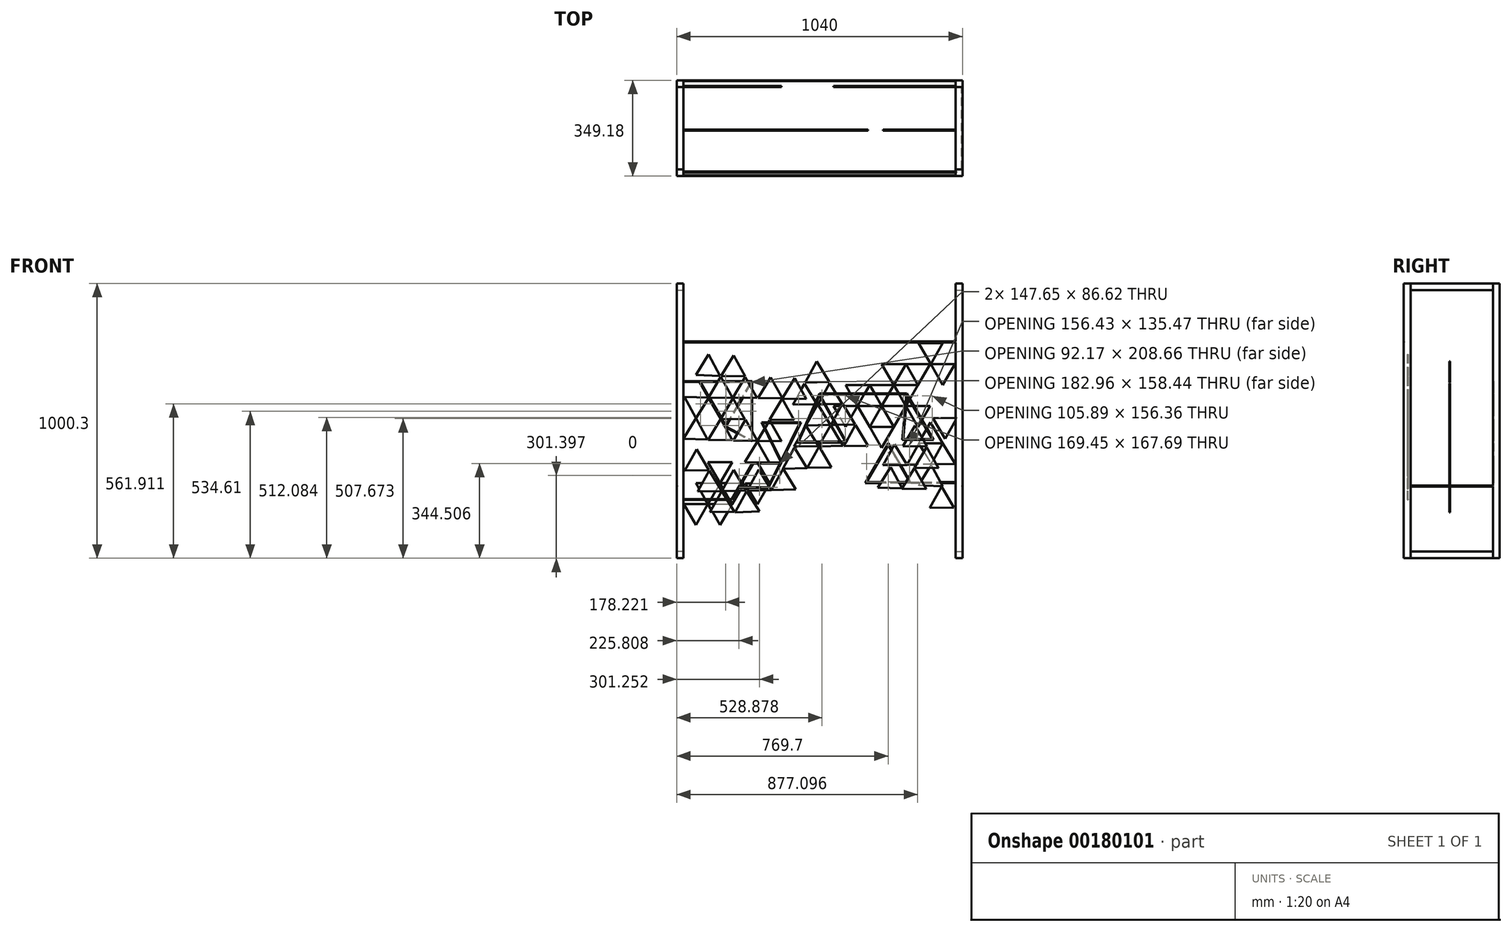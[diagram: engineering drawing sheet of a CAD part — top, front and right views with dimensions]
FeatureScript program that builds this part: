
annotation { "Feature Type Name" : "Feature", "Feature Type Description" : "" }
export const myFeature = defineFeature(function(context is Context, id is Id, definition is map)
    precondition{}
    {
        {
            var Q0;
            Q0=qCreatedBy(makeId("Front.planeOp"),FACE);
            var sketch = newSketch(context, id + "F0", { "sketchPlane" : qUnion([Q0])});
            skLineSegment(sketch, "E0.bottom", {"start": v(500, 500) * mm, "end": v(-500, 500) * mm, "construction": true});
            skLineSegment(sketch, "E0.top", {"start": v(500, -500) * mm, "end": v(-500, -500) * mm, "construction": true});
            skLineSegment(sketch, "E0.left", {"start": v(500, 500) * mm, "end": v(500, -500) * mm, "construction": true});
            skLineSegment(sketch, "E0.right", {"start": v(-500, 500) * mm, "end": v(-500, -500) * mm, "construction": true});
            skPoint(sketch, "E0.middle", {"position": v(0, 0) * mm});
            skCircle(sketch, "E1.cCircle", {"center": v(-269.92, 152.96) * mm, "radius": 25.4 * mm, "construction": true});
            skLineSegment(sketch, "E1.0", {"start": v(-268.9, 203.75) * mm, "end": v(-226.45, 126.67) * mm});
            skLineSegment(sketch, "E1.1", {"start": v(-226.45, 126.67) * mm, "end": v(-314.42, 128.45) * mm});
            skLineSegment(sketch, "E1.2", {"start": v(-314.42, 128.45) * mm, "end": v(-268.9, 203.75) * mm});
            skPoint(sketch, "E1.0.midPoint", {"position": v(-247.67, 165.2) * mm});
            skCircle(sketch, "E2.cCircle", {"center": v(-360.87, 155.69) * mm, "radius": 25.4 * mm, "construction": true});
            skLineSegment(sketch, "E2.0", {"start": v(-359.99, 206.48) * mm, "end": v(-317.33, 129.52) * mm});
            skLineSegment(sketch, "E2.1", {"start": v(-317.33, 129.52) * mm, "end": v(-405.3, 131.05) * mm});
            skLineSegment(sketch, "E2.2", {"start": v(-405.3, 131.05) * mm, "end": v(-359.99, 206.48) * mm});
            skPoint(sketch, "E2.0.midPoint", {"position": v(-338.66, 168) * mm});
            skCircle(sketch, "E3.cCircle", {"center": v(-450.9, 158.41) * mm, "radius": 25.4 * mm, "construction": true});
            skLineSegment(sketch, "E3.0", {"start": v(-449.97, 209.2) * mm, "end": v(-407.39, 132.2) * mm});
            skLineSegment(sketch, "E3.1", {"start": v(-407.39, 132.2) * mm, "end": v(-495.36, 133.83) * mm});
            skLineSegment(sketch, "E3.2", {"start": v(-495.36, 133.83) * mm, "end": v(-449.97, 209.2) * mm});
            skPoint(sketch, "E3.0.midPoint", {"position": v(-428.68, 170.7) * mm});
            skCircle(sketch, "E4.cCircle", {"center": v(-227.18, 73.83) * mm, "radius": 25.4 * mm, "construction": true});
            skLineSegment(sketch, "E4.0", {"start": v(-226.18, 124.62) * mm, "end": v(-183.7, 47.57) * mm});
            skLineSegment(sketch, "E4.1", {"start": v(-183.7, 47.57) * mm, "end": v(-271.67, 49.3) * mm});
            skLineSegment(sketch, "E4.2", {"start": v(-271.67, 49.3) * mm, "end": v(-226.18, 124.62) * mm});
            skPoint(sketch, "E4.0.midPoint", {"position": v(-204.94, 86.1) * mm});
            skCircle(sketch, "E5.cCircle", {"center": v(-182.62, 151.14) * mm, "radius": 25.4 * mm, "construction": true});
            skLineSegment(sketch, "E5.0", {"start": v(-181.92, 201.93) * mm, "end": v(-138.97, 125.14) * mm});
            skLineSegment(sketch, "E5.1", {"start": v(-138.97, 125.14) * mm, "end": v(-226.95, 126.34) * mm});
            skLineSegment(sketch, "E5.2", {"start": v(-226.95, 126.34) * mm, "end": v(-181.92, 201.93) * mm});
            skPoint(sketch, "E5.0.midPoint", {"position": v(-160.45, 163.54) * mm});
            skCircle(sketch, "E6.cCircle", {"center": v(-137.14, 229.35) * mm, "radius": 25.4 * mm, "construction": true});
            skLineSegment(sketch, "E6.0", {"start": v(-136.43, 280.15) * mm, "end": v(-93.51, 203.33) * mm});
            skLineSegment(sketch, "E6.1", {"start": v(-93.51, 203.33) * mm, "end": v(-181.49, 204.57) * mm});
            skLineSegment(sketch, "E6.2", {"start": v(-181.49, 204.57) * mm, "end": v(-136.43, 280.15) * mm});
            skPoint(sketch, "E6.0.midPoint", {"position": v(-114.97, 241.74) * mm});
            skCircle(sketch, "E7.cCircle", {"center": v(-91.67, 304.84) * mm, "radius": 25.4 * mm, "construction": true});
            skLineSegment(sketch, "E7.0", {"start": v(-91.04, 355.63) * mm, "end": v(-48, 278.9) * mm});
            skLineSegment(sketch, "E7.1", {"start": v(-48, 278.9) * mm, "end": v(-135.97, 279.98) * mm});
            skLineSegment(sketch, "E7.2", {"start": v(-135.97, 279.98) * mm, "end": v(-91.04, 355.63) * mm});
            skPoint(sketch, "E7.0.midPoint", {"position": v(-69.52, 317.27) * mm});
            skCircle(sketch, "E8.cCircle", {"center": v(-178.98, 307.57) * mm, "radius": 25.4 * mm, "construction": true});
            skLineSegment(sketch, "E8.0", {"start": v(-178.2, 358.36) * mm, "end": v(-135.38, 281.5) * mm});
            skLineSegment(sketch, "E8.1", {"start": v(-135.38, 281.5) * mm, "end": v(-223.36, 282.85) * mm});
            skLineSegment(sketch, "E8.2", {"start": v(-223.36, 282.85) * mm, "end": v(-178.2, 358.36) * mm});
            skPoint(sketch, "E8.0.midPoint", {"position": v(-156.79, 319.93) * mm});
            skCircle(sketch, "E9.cCircle", {"center": v(-315.4, 231.17) * mm, "radius": 25.4 * mm, "construction": true});
            skLineSegment(sketch, "E9.0", {"start": v(-314.62, 281.96) * mm, "end": v(-271.8, 205.1) * mm});
            skLineSegment(sketch, "E9.1", {"start": v(-271.8, 205.1) * mm, "end": v(-359.78, 206.45) * mm});
            skLineSegment(sketch, "E9.2", {"start": v(-359.78, 206.45) * mm, "end": v(-314.62, 281.96) * mm});
            skPoint(sketch, "E9.0.midPoint", {"position": v(-293.2, 243.53) * mm});
            skCircle(sketch, "E10.cCircle", {"center": v(-270.83, 308.48) * mm, "radius": 25.4 * mm, "construction": true});
            skLineSegment(sketch, "E10.0", {"start": v(-270.06, 359.27) * mm, "end": v(-227.23, 282.4) * mm});
            skLineSegment(sketch, "E10.1", {"start": v(-227.23, 282.4) * mm, "end": v(-315.21, 283.75) * mm});
            skLineSegment(sketch, "E10.2", {"start": v(-315.21, 283.75) * mm, "end": v(-270.06, 359.27) * mm});
            skPoint(sketch, "E10.0.midPoint", {"position": v(-248.64, 320.84) * mm});
            skCircle(sketch, "E11.cCircle", {"center": v(-313.58, 387.6) * mm, "radius": 25.4 * mm, "construction": true});
            skLineSegment(sketch, "E11.0", {"start": v(-312.67, 438.4) * mm, "end": v(-270.05, 361.42) * mm});
            skLineSegment(sketch, "E11.1", {"start": v(-270.05, 361.42) * mm, "end": v(-358.02, 363) * mm});
            skLineSegment(sketch, "E11.2", {"start": v(-358.02, 363) * mm, "end": v(-312.67, 438.4) * mm});
            skPoint(sketch, "E11.0.midPoint", {"position": v(-291.36, 399.9) * mm});
            skCircle(sketch, "E12.cCircle", {"center": v(-359.96, 309.39) * mm, "radius": 25.4 * mm, "construction": true});
            skLineSegment(sketch, "E12.0", {"start": v(-359.14, 360.18) * mm, "end": v(-316.38, 283.28) * mm});
            skLineSegment(sketch, "E12.1", {"start": v(-316.38, 283.28) * mm, "end": v(-404.36, 284.7) * mm});
            skLineSegment(sketch, "E12.2", {"start": v(-404.36, 284.7) * mm, "end": v(-359.14, 360.18) * mm});
            skPoint(sketch, "E12.0.midPoint", {"position": v(-337.76, 321.73) * mm});
            skCircle(sketch, "E13.cCircle", {"center": v(-448.25, 259.98) * mm, "radius": 25.4 * mm, "construction": true});
            skLineSegment(sketch, "E13.0", {"start": v(-403.42, 283.87) * mm, "end": v(-449.97, 209.2) * mm});
            skLineSegment(sketch, "E13.1", {"start": v(-449.97, 209.2) * mm, "end": v(-491.36, 286.85) * mm});
            skLineSegment(sketch, "E13.2", {"start": v(-491.36, 286.85) * mm, "end": v(-403.42, 283.87) * mm});
            skPoint(sketch, "E13.0.midPoint", {"position": v(-426.7, 246.54) * mm});
            skCircle(sketch, "E14.cCircle", {"center": v(-405.43, 390.33) * mm, "radius": 25.4 * mm, "construction": true});
            skLineSegment(sketch, "E14.0", {"start": v(-403.66, 441.1) * mm, "end": v(-362.36, 363.4) * mm});
            skLineSegment(sketch, "E14.1", {"start": v(-362.36, 363.4) * mm, "end": v(-450.29, 366.48) * mm});
            skLineSegment(sketch, "E14.2", {"start": v(-450.29, 366.48) * mm, "end": v(-403.66, 441.1) * mm});
            skPoint(sketch, "E14.0.midPoint", {"position": v(-383, 402.25) * mm});
            skCircle(sketch, "E15.cCircle", {"center": v(389.15, 53.61) * mm, "radius": 25.4 * mm, "construction": true});
            skLineSegment(sketch, "E15.0", {"start": v(389.72, 104.4) * mm, "end": v(432.85, 27.72) * mm});
            skLineSegment(sketch, "E15.1", {"start": v(432.85, 27.72) * mm, "end": v(344.87, 28.71) * mm});
            skLineSegment(sketch, "E15.2", {"start": v(344.87, 28.71) * mm, "end": v(389.72, 104.4) * mm});
            skPoint(sketch, "E15.0.midPoint", {"position": v(411.29, 66.06) * mm});
            skCircle(sketch, "E16.cCircle", {"center": v(456.43, 185.05) * mm, "radius": 25.4 * mm, "construction": true});
            skLineSegment(sketch, "E16.0", {"start": v(412.02, 209.72) * mm, "end": v(500, 211.17) * mm});
            skLineSegment(sketch, "E16.1", {"start": v(500, 211.17) * mm, "end": v(457.27, 134.26) * mm});
            skLineSegment(sketch, "E16.2", {"start": v(457.27, 134.26) * mm, "end": v(412.02, 209.72) * mm});
            skPoint(sketch, "E16.0.midPoint", {"position": v(456.01, 210.45) * mm});
            skCircle(sketch, "E17.cCircle", {"center": v(347.31, 131.83) * mm, "radius": 25.4 * mm, "construction": true});
            skLineSegment(sketch, "E17.0", {"start": v(348.1, 182.62) * mm, "end": v(390.91, 105.75) * mm});
            skLineSegment(sketch, "E17.1", {"start": v(390.91, 105.75) * mm, "end": v(302.93, 107.1) * mm});
            skLineSegment(sketch, "E17.2", {"start": v(302.93, 107.1) * mm, "end": v(348.1, 182.62) * mm});
            skPoint(sketch, "E17.0.midPoint", {"position": v(369.5, 144.19) * mm});
            skCircle(sketch, "E18.cCircle", {"center": v(344.43, -22.63) * mm, "radius": 25.4 * mm, "construction": true});
            skLineSegment(sketch, "E18.0", {"start": v(345.1, 28.16) * mm, "end": v(388.08, -48.61) * mm});
            skLineSegment(sketch, "E18.1", {"start": v(388.08, -48.61) * mm, "end": v(300.1, -47.45) * mm});
            skLineSegment(sketch, "E18.2", {"start": v(300.1, -47.45) * mm, "end": v(345.1, 28.16) * mm});
            skPoint(sketch, "E18.0.midPoint", {"position": v(366.6, -10.22) * mm});
            skCircle(sketch, "E19.cCircle", {"center": v(257.12, -19.9) * mm, "radius": 25.4 * mm, "construction": true});
            skLineSegment(sketch, "E19.0", {"start": v(258.54, 30.88) * mm, "end": v(300.39, -46.53) * mm});
            skLineSegment(sketch, "E19.1", {"start": v(300.39, -46.53) * mm, "end": v(212.43, -44.06) * mm});
            skLineSegment(sketch, "E19.2", {"start": v(212.43, -44.06) * mm, "end": v(258.54, 30.88) * mm});
            skPoint(sketch, "E19.0.midPoint", {"position": v(279.47, -7.83) * mm});
            skSolve(sketch);
        }
        {
            var Q0;
            Q0=makeQuery(id+"F0.imprint","IMPRINT",FACE,{"disambiguationData":[TD([[makeQuery(id+"F0.imprint","IMPRINT",EDGE,{"derivedFrom":sQuery(id+"F0.wireOp",EDGE,"E14.0")}),-1.0]])]});
            var Q1;
            Q1=makeQuery(id+"F0.imprint","IMPRINT",FACE,{"disambiguationData":[TD([[makeQuery(id+"F0.imprint","IMPRINT",EDGE,{"derivedFrom":sQuery(id+"F0.wireOp",EDGE,"E11.0")}),-1.0]])]});
            var Q2;
            Q2=makeQuery(id+"F0.imprint","IMPRINT",FACE,{"disambiguationData":[TD([[makeQuery(id+"F0.imprint","IMPRINT",EDGE,{"derivedFrom":sQuery(id+"F0.wireOp",EDGE,"E12.0")}),-1.0]])]});
            var Q3;
            Q3=makeQuery(id+"F0.imprint","IMPRINT",FACE,{"disambiguationData":[TD([[makeQuery(id+"F0.imprint","IMPRINT",EDGE,{"derivedFrom":sQuery(id+"F0.wireOp",EDGE,"E13.0")}),-1.0]])]});
            var Q4;
            Q4=makeQuery(id+"F0.imprint","IMPRINT",FACE,{"disambiguationData":[TD([[makeQuery(id+"F0.imprint","IMPRINT",EDGE,{"derivedFrom":sQuery(id+"F0.wireOp",EDGE,"E3.0")}),-1.0]])]});
            var Q5;
            Q5=makeQuery(id+"F0.imprint","IMPRINT",FACE,{"disambiguationData":[TD([[makeQuery(id+"F0.imprint","IMPRINT",EDGE,{"derivedFrom":sQuery(id+"F0.wireOp",EDGE,"E2.0")}),-1.0]])]});
            var Q6;
            Q6=makeQuery(id+"F0.imprint","IMPRINT",FACE,{"disambiguationData":[TD([[makeQuery(id+"F0.imprint","IMPRINT",EDGE,{"derivedFrom":sQuery(id+"F0.wireOp",EDGE,"E9.0")}),-1.0]])]});
            var Q7;
            Q7=makeQuery(id+"F0.imprint","IMPRINT",FACE,{"disambiguationData":[TD([[makeQuery(id+"F0.imprint","IMPRINT",EDGE,{"derivedFrom":sQuery(id+"F0.wireOp",EDGE,"E10.0")}),-1.0]])]});
            var Q8;
            Q8=makeQuery(id+"F0.imprint","IMPRINT",FACE,{"disambiguationData":[TD([[makeQuery(id+"F0.imprint","IMPRINT",EDGE,{"derivedFrom":sQuery(id+"F0.wireOp",EDGE,"E8.0")}),-1.0]])]});
            var Q9;
            Q9=makeQuery(id+"F0.imprint","IMPRINT",FACE,{"disambiguationData":[TD([[makeQuery(id+"F0.imprint","IMPRINT",EDGE,{"derivedFrom":sQuery(id+"F0.wireOp",EDGE,"E7.0")}),-1.0]])]});
            var Q10;
            Q10=makeQuery(id+"F0.imprint","IMPRINT",FACE,{"disambiguationData":[TD([[makeQuery(id+"F0.imprint","IMPRINT",EDGE,{"derivedFrom":sQuery(id+"F0.wireOp",EDGE,"E6.0")}),-1.0]])]});
            var Q11;
            {var subQ1=sQuery(id+"F0.wireOp",EDGE,"E5.0");Q11=makeQuery(id+"F0.imprint","IMPRINT",FACE,{"disambiguationData":[TD([[makeQuery(id+"F0.imprint","IMPRINT",EDGE,{"derivedFrom":subQ1}),-1.0]])]});}
            var Q12;
            {var subQ0=sQuery(id+"F0.wireOp",EDGE,"E1.2");Q12=makeQuery(id+"F0.imprint","IMPRINT",FACE,{"disambiguationData":[TD([[makeQuery(id+"F0.imprint","IMPRINT",EDGE,{"derivedFrom":subQ0}),-1.0]])]});}
            var Q13;
            Q13=makeQuery(id+"F0.imprint","IMPRINT",FACE,{"disambiguationData":[TD([[makeQuery(id+"F0.imprint","IMPRINT",EDGE,{"derivedFrom":sQuery(id+"F0.wireOp",EDGE,"E4.0")}),-1.0]])]});
            var Q14;
            Q14=makeQuery(id+"F0.imprint","IMPRINT",FACE,{"disambiguationData":[TD([[makeQuery(id+"F0.imprint","IMPRINT",EDGE,{"derivedFrom":sQuery(id+"F0.wireOp",EDGE,"E17.0")}),-1.0]])]});
            var Q15;
            Q15=makeQuery(id+"F0.imprint","IMPRINT",FACE,{"disambiguationData":[TD([[makeQuery(id+"F0.imprint","IMPRINT",EDGE,{"derivedFrom":sQuery(id+"F0.wireOp",EDGE,"E16.0")}),-1.0]])]});
            var Q16;
            Q16=makeQuery(id+"F0.imprint","IMPRINT",FACE,{"disambiguationData":[TD([[makeQuery(id+"F0.imprint","IMPRINT",EDGE,{"derivedFrom":sQuery(id+"F0.wireOp",EDGE,"E15.0")}),-1.0]])]});
            var Q17;
            Q17=makeQuery(id+"F0.imprint","IMPRINT",FACE,{"disambiguationData":[TD([[makeQuery(id+"F0.imprint","IMPRINT",EDGE,{"derivedFrom":sQuery(id+"F0.wireOp",EDGE,"E18.0")}),-1.0]])]});
            var Q18;
            Q18=makeQuery(id+"F0.imprint","IMPRINT",FACE,{"disambiguationData":[TD([[makeQuery(id+"F0.imprint","IMPRINT",EDGE,{"derivedFrom":sQuery(id+"F0.wireOp",EDGE,"E19.0")}),-1.0]])]});
            extrude(context, id + "F1", {"entities" : qUnion([Q0, Q1, Q2, Q3, Q4, Q5, Q6, Q7, Q8, Q9, Q10, Q11, Q12, Q13, Q14, Q15, Q16, Q17, Q18]), "depth" : 3 * mm});
        }
        {
            var Q0;
            Q0=qCreatedBy(makeId("Top.planeOp"),FACE);
            cPlane(context, id + "F2", {"entities" : qUnion([Q0]), "cplaneType" : CPlaneType.OFFSET, "offset" : 500 * mm, "width" : 152.4 * mm, "height" : 152.4 * mm});
        }
        {
            var Q0;
            Q0=qCreatedBy(id+"F2.planeOp",FACE);
            var sketch = newSketch(context, id + "F3", { "sketchPlane" : qUnion([Q0])});
            skLineSegment(sketch, "E20.bottom", {"start": v(-520, 8.18) * mm, "end": v(-495, 8.18) * mm});
            skLineSegment(sketch, "E20.top", {"start": v(-520, -16.82) * mm, "end": v(-495, -16.82) * mm});
            skLineSegment(sketch, "E20.left", {"start": v(-520, 8.18) * mm, "end": v(-520, -16.82) * mm});
            skLineSegment(sketch, "E20.right", {"start": v(-495, 8.18) * mm, "end": v(-495, -16.82) * mm});
            skLineSegment(sketch, "E21", {"start": v(0, 81.2) * mm, "end": v(0, -142.37) * mm, "construction": true});
            skLineSegment(sketch, "E22.MirrorCS", {"start": v(520, -16.82) * mm, "end": v(495, -16.82) * mm});
            skLineSegment(sketch, "E23.MirrorCS", {"start": v(495, 8.18) * mm, "end": v(495, -16.82) * mm});
            skLineSegment(sketch, "E24.MirrorCS", {"start": v(520, 8.18) * mm, "end": v(495, 8.18) * mm});
            skLineSegment(sketch, "E25.MirrorCS", {"start": v(520, 8.18) * mm, "end": v(520, -16.82) * mm});
            skSolve(sketch);
        }
        {
            var Q0;
            Q0 = qSketchRegion(id + "F3", true);
            extrude(context, id + "F4", {"entities" : qUnion([Q0]), "oppositeDirection" : true, "depth" : 800 * mm, "hasSecondDirection" : true, "secondDirectionOppositeDirection" : false, "secondDirectionDepth" : 200 * mm});
        }
        {
            var Q0;
            Q0=makeQuery(id+"F4.opExtrude","SWEPT_FACE",FACE,{"disambiguationData":[OSD([sQuery(id+"F3.wireOp",EDGE,"E20.bottom")])]});
            var sketch = newSketch(context, id + "F5", { "sketchPlane" : qUnion([Q0])});
            skLineSegment(sketch, "E26.bottom", {"start": v(-495.28, -300.3) * mm, "end": v(-519.46, -300.3) * mm});
            skLineSegment(sketch, "E26.top", {"start": v(-495.28, -276.12) * mm, "end": v(-519.46, -276.12) * mm});
            skLineSegment(sketch, "E26.left", {"start": v(-495.28, -300.3) * mm, "end": v(-495.28, -276.12) * mm});
            skLineSegment(sketch, "E26.right", {"start": v(-519.46, -300.3) * mm, "end": v(-519.46, -276.12) * mm});
            skLineSegment(sketch, "E27", {"start": v(0, 0) * mm, "end": v(0, -471.83) * mm, "construction": true});
            skLineSegment(sketch, "E28.MirrorCS", {"start": v(495.28, -276.12) * mm, "end": v(519.46, -276.12) * mm});
            skLineSegment(sketch, "E29.MirrorCS", {"start": v(495.28, -300.3) * mm, "end": v(495.28, -276.12) * mm});
            skLineSegment(sketch, "E30.MirrorCS", {"start": v(495.28, -300.3) * mm, "end": v(519.46, -300.3) * mm});
            skLineSegment(sketch, "E31.MirrorCS", {"start": v(519.46, -300.3) * mm, "end": v(519.46, -276.12) * mm});
            skSolve(sketch);
        }
        {
            var Q0;
            Q0=makeQuery(id+"F5.imprint","IMPRINT",FACE,{"disambiguationData":[TD([[makeQuery(id+"F5.imprint","IMPRINT",EDGE,{"derivedFrom":sQuery(id+"F5.wireOp",EDGE,"E26.bottom")}),-1.0]])]});
            var Q1;
            {var subQ0=sQuery(id+"F5.wireOp",EDGE,"E28.MirrorCS");Q1=makeQuery(id+"F5.imprint","IMPRINT",FACE,{"disambiguationData":[TD([[makeQuery(id+"F5.imprint","IMPRINT",EDGE,{"derivedFrom":subQ0}),-1.0]])]});}
            extrude(context, id + "F6", {"entities" : qUnion([Q0, Q1]), "depth" : 300 * mm});
        }
        {
            var Q0;
            Q0=makeQuery(id+"F6.opExtrude","SWEPT_FACE",FACE,{"disambiguationData":[OSD([sQuery(id+"F5.wireOp",EDGE,"E26.bottom")])]});
            var sketch = newSketch(context, id + "F7", { "sketchPlane" : qUnion([Q0])});
            skLineSegment(sketch, "E32.bottom", {"start": v(-519.86, -308.03) * mm, "end": v(-495.5, -308.03) * mm});
            skLineSegment(sketch, "E32.top", {"start": v(-519.86, -332.36) * mm, "end": v(-495.5, -332.36) * mm});
            skLineSegment(sketch, "E32.left", {"start": v(-519.86, -308.03) * mm, "end": v(-519.86, -332.36) * mm});
            skLineSegment(sketch, "E32.right", {"start": v(-495.5, -308.03) * mm, "end": v(-495.5, -332.36) * mm});
            skLineSegment(sketch, "E33", {"start": v(0, 0) * mm, "end": v(0, -208.74) * mm, "construction": true});
            skLineSegment(sketch, "E34.MirrorCS", {"start": v(519.86, -308.03) * mm, "end": v(495.5, -308.03) * mm});
            skLineSegment(sketch, "E35.MirrorCS", {"start": v(519.86, -332.36) * mm, "end": v(495.5, -332.36) * mm});
            skLineSegment(sketch, "E36.MirrorCS", {"start": v(495.5, -308.03) * mm, "end": v(495.5, -332.36) * mm});
            skLineSegment(sketch, "E37.MirrorCS", {"start": v(519.86, -308.03) * mm, "end": v(519.86, -332.36) * mm});
            skSolve(sketch);
        }
        {
            var Q0;
            {var subQ2=sQuery(id+"F7.wireOp",EDGE,"E35.MirrorCS");Q0=makeQuery(id+"F7.imprint","IMPRINT",FACE,{"disambiguationData":[TD([[makeQuery(id+"F7.imprint","IMPRINT",EDGE,{"derivedFrom":subQ2}),-1.0]])]});}
            var Q1;
            Q1=makeQuery(id+"F7.imprint","IMPRINT",FACE,{"disambiguationData":[TD([[makeQuery(id+"F7.imprint","IMPRINT",EDGE,{"derivedFrom":sQuery(id+"F7.wireOp",EDGE,"E32.bottom")}),-1.0]])]});
            extrude(context, id + "F8", {"entities" : qUnion([Q0, Q1]), "oppositeDirection" : true, "depth" : 1000 * mm});
        }
        {
            var Q0;
            Q0=makeQuery(id+"F8.opExtrude","SWEPT_FACE",FACE,{"disambiguationData":[OSD([sQuery(id+"F5.wireOp",EDGE,"E26.bottom")])]});
            var sketch = newSketch(context, id + "F9", { "sketchPlane" : qUnion([Q0])});
            skCircle(sketch, "E38.cCircle", {"center": v(138.38, 304.83) * mm, "radius": 25.4 * mm, "construction": true});
            skLineSegment(sketch, "E38.0", {"start": v(94.39, 330.23) * mm, "end": v(182.38, 330.23) * mm});
            skLineSegment(sketch, "E38.1", {"start": v(182.38, 330.23) * mm, "end": v(138.38, 254.03) * mm});
            skLineSegment(sketch, "E38.2", {"start": v(138.38, 254.03) * mm, "end": v(94.39, 330.23) * mm});
            skPoint(sketch, "E38.0.midPoint", {"position": v(138.38, 330.23) * mm});
            skCircle(sketch, "E39.cCircle", {"center": v(226.37, 304.83) * mm, "radius": 25.4 * mm, "construction": true});
            skLineSegment(sketch, "E39.0", {"start": v(182.38, 330.23) * mm, "end": v(270.37, 330.23) * mm});
            skLineSegment(sketch, "E39.1", {"start": v(270.37, 330.23) * mm, "end": v(226.37, 254.03) * mm});
            skLineSegment(sketch, "E39.2", {"start": v(226.37, 254.03) * mm, "end": v(182.38, 330.23) * mm});
            skPoint(sketch, "E39.0.midPoint", {"position": v(226.37, 330.23) * mm});
            skCircle(sketch, "E40.cCircle", {"center": v(182.38, 228.63) * mm, "radius": 25.4 * mm, "construction": true});
            skLineSegment(sketch, "E40.0", {"start": v(138.38, 254.03) * mm, "end": v(226.37, 254.03) * mm});
            skLineSegment(sketch, "E40.1", {"start": v(226.37, 254.03) * mm, "end": v(182.38, 177.83) * mm});
            skLineSegment(sketch, "E40.2", {"start": v(182.38, 177.83) * mm, "end": v(138.38, 254.03) * mm});
            skPoint(sketch, "E40.0.midPoint", {"position": v(182.38, 254.03) * mm});
            skCircle(sketch, "E41.cCircle", {"center": v(226.37, 152.43) * mm, "radius": 25.4 * mm, "construction": true});
            skLineSegment(sketch, "E41.0", {"start": v(182.38, 177.83) * mm, "end": v(270.37, 177.83) * mm});
            skLineSegment(sketch, "E41.1", {"start": v(270.37, 177.83) * mm, "end": v(226.37, 101.63) * mm});
            skLineSegment(sketch, "E41.2", {"start": v(226.37, 101.63) * mm, "end": v(182.38, 177.83) * mm});
            skPoint(sketch, "E41.0.midPoint", {"position": v(226.37, 177.83) * mm});
            skCircle(sketch, "E42.cCircle", {"center": v(94.39, 228.63) * mm, "radius": 25.4 * mm, "construction": true});
            skLineSegment(sketch, "E42.0", {"start": v(50.4, 254.03) * mm, "end": v(138.38, 254.03) * mm});
            skLineSegment(sketch, "E42.1", {"start": v(138.38, 254.03) * mm, "end": v(94.39, 177.83) * mm});
            skLineSegment(sketch, "E42.2", {"start": v(94.39, 177.83) * mm, "end": v(50.4, 254.03) * mm});
            skPoint(sketch, "E42.0.midPoint", {"position": v(94.39, 254.03) * mm});
            skCircle(sketch, "E43.cCircle", {"center": v(270.37, 228.63) * mm, "radius": 25.4 * mm, "construction": true});
            skLineSegment(sketch, "E43.0", {"start": v(226.37, 254.03) * mm, "end": v(314.36, 254.03) * mm});
            skLineSegment(sketch, "E43.1", {"start": v(314.36, 254.03) * mm, "end": v(270.37, 177.83) * mm});
            skLineSegment(sketch, "E43.2", {"start": v(270.37, 177.83) * mm, "end": v(226.37, 254.03) * mm});
            skPoint(sketch, "E43.0.midPoint", {"position": v(270.37, 254.03) * mm});
            skCircle(sketch, "E44.cCircle", {"center": v(314.36, 304.83) * mm, "radius": 25.4 * mm, "construction": true});
            skLineSegment(sketch, "E44.0", {"start": v(270.37, 330.23) * mm, "end": v(358.35, 330.23) * mm});
            skLineSegment(sketch, "E44.1", {"start": v(358.35, 330.23) * mm, "end": v(314.36, 254.03) * mm});
            skLineSegment(sketch, "E44.2", {"start": v(314.36, 254.03) * mm, "end": v(270.37, 330.23) * mm});
            skPoint(sketch, "E44.0.midPoint", {"position": v(314.36, 330.23) * mm});
            skCircle(sketch, "E45.cCircle", {"center": v(358.35, 228.63) * mm, "radius": 25.4 * mm, "construction": true});
            skLineSegment(sketch, "E45.0", {"start": v(314.36, 254.03) * mm, "end": v(402.35, 254.03) * mm});
            skLineSegment(sketch, "E45.1", {"start": v(402.35, 254.03) * mm, "end": v(358.35, 177.83) * mm});
            skLineSegment(sketch, "E45.2", {"start": v(358.35, 177.83) * mm, "end": v(314.36, 254.03) * mm});
            skPoint(sketch, "E45.0.midPoint", {"position": v(358.35, 254.03) * mm});
            skCircle(sketch, "E46.cCircle", {"center": v(270.37, 381.03) * mm, "radius": 25.4 * mm, "construction": true});
            skLineSegment(sketch, "E46.0", {"start": v(226.37, 406.43) * mm, "end": v(314.36, 406.43) * mm});
            skLineSegment(sketch, "E46.1", {"start": v(314.36, 406.43) * mm, "end": v(270.37, 330.23) * mm});
            skLineSegment(sketch, "E46.2", {"start": v(270.37, 330.23) * mm, "end": v(226.37, 406.43) * mm});
            skPoint(sketch, "E46.0.midPoint", {"position": v(270.37, 406.43) * mm});
            skCircle(sketch, "E47.cCircle", {"center": v(358.35, 381.03) * mm, "radius": 25.4 * mm, "construction": true});
            skLineSegment(sketch, "E47.0", {"start": v(314.36, 406.43) * mm, "end": v(402.35, 406.43) * mm});
            skLineSegment(sketch, "E47.1", {"start": v(402.35, 406.43) * mm, "end": v(358.35, 330.23) * mm});
            skLineSegment(sketch, "E47.2", {"start": v(358.35, 330.23) * mm, "end": v(314.36, 406.43) * mm});
            skPoint(sketch, "E47.0.midPoint", {"position": v(358.35, 406.43) * mm});
            skCircle(sketch, "E48.cCircle", {"center": v(448.6, 381.03) * mm, "radius": 25.4 * mm, "construction": true});
            skLineSegment(sketch, "E48.0", {"start": v(404.6, 406.43) * mm, "end": v(492.59, 406.43) * mm});
            skLineSegment(sketch, "E48.1", {"start": v(492.59, 406.43) * mm, "end": v(448.6, 330.23) * mm});
            skLineSegment(sketch, "E48.2", {"start": v(448.6, 330.23) * mm, "end": v(404.6, 406.43) * mm});
            skPoint(sketch, "E48.0.midPoint", {"position": v(448.6, 406.43) * mm});
            skCircle(sketch, "E49.cCircle", {"center": v(404.6, 457.23) * mm, "radius": 25.4 * mm, "construction": true});
            skLineSegment(sketch, "E49.0", {"start": v(360.6, 482.63) * mm, "end": v(448.6, 482.63) * mm});
            skLineSegment(sketch, "E49.1", {"start": v(448.6, 482.63) * mm, "end": v(404.6, 406.43) * mm});
            skLineSegment(sketch, "E49.2", {"start": v(404.6, 406.43) * mm, "end": v(360.6, 482.63) * mm});
            skPoint(sketch, "E49.0.midPoint", {"position": v(404.6, 482.63) * mm});
            skCircle(sketch, "E50.cCircle", {"center": v(-450.1, -128.73) * mm, "radius": 25.4 * mm, "construction": true});
            skLineSegment(sketch, "E50.0", {"start": v(-494.1, -103.33) * mm, "end": v(-406.1, -103.33) * mm});
            skLineSegment(sketch, "E50.1", {"start": v(-406.1, -103.33) * mm, "end": v(-450.1, -179.53) * mm});
            skLineSegment(sketch, "E50.2", {"start": v(-450.1, -179.53) * mm, "end": v(-494.1, -103.33) * mm});
            skPoint(sketch, "E50.0.midPoint", {"position": v(-450.1, -103.33) * mm});
            skCircle(sketch, "E51.cCircle", {"center": v(-406.1, -52.53) * mm, "radius": 25.4 * mm, "construction": true});
            skLineSegment(sketch, "E51.0", {"start": v(-450.1, -27.13) * mm, "end": v(-362.1, -27.13) * mm});
            skLineSegment(sketch, "E51.1", {"start": v(-362.1, -27.13) * mm, "end": v(-406.1, -103.33) * mm});
            skLineSegment(sketch, "E51.2", {"start": v(-406.1, -103.33) * mm, "end": v(-450.1, -27.13) * mm});
            skPoint(sketch, "E51.0.midPoint", {"position": v(-406.1, -27.13) * mm});
            skCircle(sketch, "E52.cCircle", {"center": v(-362.1, -128.73) * mm, "radius": 25.4 * mm, "construction": true});
            skLineSegment(sketch, "E52.0", {"start": v(-406.1, -103.33) * mm, "end": v(-318.12, -103.33) * mm});
            skLineSegment(sketch, "E52.1", {"start": v(-318.12, -103.33) * mm, "end": v(-362.1, -179.53) * mm});
            skLineSegment(sketch, "E52.2", {"start": v(-362.1, -179.53) * mm, "end": v(-406.1, -103.33) * mm});
            skPoint(sketch, "E52.0.midPoint", {"position": v(-362.1, -103.33) * mm});
            skCircle(sketch, "E53.cCircle", {"center": v(-362.1, 23.67) * mm, "radius": 25.4 * mm, "construction": true});
            skLineSegment(sketch, "E53.0", {"start": v(-406.1, 49.07) * mm, "end": v(-318.12, 49.07) * mm});
            skLineSegment(sketch, "E53.1", {"start": v(-318.12, 49.07) * mm, "end": v(-362.1, -27.13) * mm});
            skLineSegment(sketch, "E53.2", {"start": v(-362.1, -27.13) * mm, "end": v(-406.1, 49.07) * mm});
            skPoint(sketch, "E53.0.midPoint", {"position": v(-362.1, 49.07) * mm});
            skCircle(sketch, "E54.cCircle", {"center": v(-318.12, -52.53) * mm, "radius": 25.4 * mm, "construction": true});
            skLineSegment(sketch, "E54.0", {"start": v(-362.1, -27.13) * mm, "end": v(-274.12, -27.13) * mm});
            skLineSegment(sketch, "E54.1", {"start": v(-274.12, -27.13) * mm, "end": v(-318.12, -103.33) * mm});
            skLineSegment(sketch, "E54.2", {"start": v(-318.12, -103.33) * mm, "end": v(-362.1, -27.13) * mm});
            skPoint(sketch, "E54.0.midPoint", {"position": v(-318.12, -27.13) * mm});
            skCircle(sketch, "E55.cCircle", {"center": v(-226.16, -53.53) * mm, "radius": 25.4 * mm, "construction": true});
            skLineSegment(sketch, "E55.0", {"start": v(-270.15, -28.13) * mm, "end": v(-182.16, -28.13) * mm});
            skLineSegment(sketch, "E55.1", {"start": v(-182.16, -28.13) * mm, "end": v(-226.16, -104.33) * mm});
            skLineSegment(sketch, "E55.2", {"start": v(-226.16, -104.33) * mm, "end": v(-270.15, -28.13) * mm});
            skPoint(sketch, "E55.0.midPoint", {"position": v(-226.16, -28.13) * mm});
            skCircle(sketch, "E56.cCircle", {"center": v(-182.16, 22.67) * mm, "radius": 25.4 * mm, "construction": true});
            skLineSegment(sketch, "E56.0", {"start": v(-226.16, 48.07) * mm, "end": v(-138.17, 48.07) * mm});
            skLineSegment(sketch, "E56.1", {"start": v(-138.17, 48.07) * mm, "end": v(-182.16, -28.13) * mm});
            skLineSegment(sketch, "E56.2", {"start": v(-182.16, -28.13) * mm, "end": v(-226.16, 48.07) * mm});
            skPoint(sketch, "E56.0.midPoint", {"position": v(-182.16, 48.07) * mm});
            skSolve(sketch);
        }
        {
            var Q0;
            Q0=makeQuery(id+"F8.opExtrude","SWEPT_FACE",FACE,{"disambiguationData":[OSD([sQuery(id+"F5.wireOp",EDGE,"E26.bottom")])]});
            var sketch = newSketch(context, id + "F10", { "sketchPlane" : qUnion([Q0])});
            skSolve(sketch);
        }
        {
            var Q0;
            Q0=makeQuery(id+"F9.imprint","IMPRINT",FACE,{"disambiguationData":[TD([[makeQuery(id+"F9.imprint","IMPRINT",EDGE,{"derivedFrom":sQuery(id+"F9.wireOp",EDGE,"E42.0")}),-1.0]])]});
            var Q1;
            Q1=makeQuery(id+"F9.imprint","IMPRINT",FACE,{"disambiguationData":[TD([[makeQuery(id+"F9.imprint","IMPRINT",EDGE,{"derivedFrom":sQuery(id+"F9.wireOp",EDGE,"E45.0")}),-1.0]])]});
            var Q2;
            Q2=makeQuery(id+"F9.imprint","IMPRINT",FACE,{"disambiguationData":[TD([[makeQuery(id+"F9.imprint","IMPRINT",EDGE,{"derivedFrom":sQuery(id+"F9.wireOp",EDGE,"E49.0")}),-1.0]])]});
            var Q3;
            Q3=makeQuery(id+"F9.imprint","IMPRINT",FACE,{"disambiguationData":[TD([[makeQuery(id+"F9.imprint","IMPRINT",EDGE,{"derivedFrom":sQuery(id+"F9.wireOp",EDGE,"E50.0")}),-1.0]])]});
            var Q4;
            Q4=makeQuery(id+"F9.imprint","IMPRINT",FACE,{"disambiguationData":[TD([[makeQuery(id+"F9.imprint","IMPRINT",EDGE,{"derivedFrom":sQuery(id+"F9.wireOp",EDGE,"E53.0")}),-1.0]])]});
            var Q5;
            Q5=makeQuery(id+"F9.imprint","IMPRINT",FACE,{"disambiguationData":[TD([[makeQuery(id+"F9.imprint","IMPRINT",EDGE,{"derivedFrom":sQuery(id+"F9.wireOp",EDGE,"E55.0")}),-1.0]])]});
            var Q6;
            Q6=makeQuery(id+"F9.imprint","IMPRINT",FACE,{"disambiguationData":[TD([[makeQuery(id+"F9.imprint","IMPRINT",EDGE,{"derivedFrom":sQuery(id+"F9.wireOp",EDGE,"E56.0")}),-1.0]])]});
            var Q7;
            Q7=makeQuery(id+"F9.imprint","IMPRINT",FACE,{"disambiguationData":[TD([[makeQuery(id+"F9.imprint","IMPRINT",EDGE,{"derivedFrom":sQuery(id+"F9.wireOp",EDGE,"E38.0")}),-1.0]])]});
            var Q8;
            Q8=makeQuery(id+"F9.imprint","IMPRINT",FACE,{"disambiguationData":[TD([[makeQuery(id+"F9.imprint","IMPRINT",EDGE,{"derivedFrom":sQuery(id+"F9.wireOp",EDGE,"E41.0")}),-1.0]])]});
            var Q9;
            Q9=makeQuery(id+"F9.imprint","IMPRINT",FACE,{"disambiguationData":[TD([[makeQuery(id+"F9.imprint","IMPRINT",EDGE,{"derivedFrom":sQuery(id+"F9.wireOp",EDGE,"E46.0")}),-1.0]])]});
            var Q10;
            Q10=makeQuery(id+"F9.imprint","IMPRINT",FACE,{"disambiguationData":[TD([[makeQuery(id+"F9.imprint","IMPRINT",EDGE,{"derivedFrom":sQuery(id+"F9.wireOp",EDGE,"E47.0")}),-1.0]])]});
            var Q11;
            Q11=makeQuery(id+"F9.imprint","IMPRINT",FACE,{"disambiguationData":[TD([[makeQuery(id+"F9.imprint","IMPRINT",EDGE,{"derivedFrom":sQuery(id+"F9.wireOp",EDGE,"E51.0")}),-1.0]])]});
            var Q12;
            Q12=makeQuery(id+"F9.imprint","IMPRINT",FACE,{"disambiguationData":[TD([[makeQuery(id+"F9.imprint","IMPRINT",EDGE,{"derivedFrom":sQuery(id+"F9.wireOp",EDGE,"E52.0")}),-1.0]])]});
            var Q13;
            Q13=makeQuery(id+"F9.imprint","IMPRINT",FACE,{"disambiguationData":[TD([[makeQuery(id+"F9.imprint","IMPRINT",EDGE,{"derivedFrom":sQuery(id+"F9.wireOp",EDGE,"E54.0")}),-1.0]])]});
            var Q14;
            Q14=makeQuery(id+"F9.imprint","IMPRINT",FACE,{"disambiguationData":[TD([[makeQuery(id+"F9.imprint","IMPRINT",EDGE,{"derivedFrom":sQuery(id+"F9.wireOp",EDGE,"E39.0")}),-1.0]])]});
            var Q15;
            Q15=makeQuery(id+"F9.imprint","IMPRINT",FACE,{"disambiguationData":[TD([[makeQuery(id+"F9.imprint","IMPRINT",EDGE,{"derivedFrom":sQuery(id+"F9.wireOp",EDGE,"E40.0")}),-1.0]])]});
            var Q16;
            Q16=makeQuery(id+"F9.imprint","IMPRINT",FACE,{"disambiguationData":[TD([[makeQuery(id+"F9.imprint","IMPRINT",EDGE,{"derivedFrom":sQuery(id+"F9.wireOp",EDGE,"E43.0")}),-1.0]])]});
            var Q17;
            Q17=makeQuery(id+"F9.imprint","IMPRINT",FACE,{"disambiguationData":[TD([[makeQuery(id+"F9.imprint","IMPRINT",EDGE,{"derivedFrom":sQuery(id+"F9.wireOp",EDGE,"E44.0")}),-1.0]])]});
            var Q18;
            {var subQ0=sQuery(id+"F9.wireOp",EDGE,"E48.2");Q18=makeQuery(id+"F9.imprint","IMPRINT",FACE,{"disambiguationData":[TD([[makeQuery(id+"F9.imprint","IMPRINT",EDGE,{"derivedFrom":subQ0}),-1.0]])]});}
            var Q19;
            {var subQ0=sQuery(id+"F9.wireOp",EDGE,"E48.1");var subQ1=sQuery(id+"F9.wireOp",EDGE,"E48.0");var subQ2=makeQuery(id+"F9.imprint","INTERSECT",VERTEX,{"derivedFrom":[subQ1,subQ0]});Q19=makeQuery(id+"F9.imprint","IMPRINT",FACE,{"disambiguationData":[TD([[makeQuery(id+"F9.imprint","IMPRINT",EDGE,{"disambiguationData":[TD([[subQ2,1.0]])],"derivedFrom":subQ1}),-1.0]])]});}
            extrude(context, id + "F11", {"entities" : qUnion([Q0, Q1, Q2, Q3, Q4, Q5, Q6, Q7, Q8, Q9, Q10, Q11, Q12, Q13, Q14, Q15, Q16, Q17, Q18, Q19]), "operationType" : NewBodyOperationType.ADD, "oppositeDirection" : true, "depth" : 3 * mm});
        }
        {
            var Q0;
            Q0=makeQuery(id+"F8.opExtrude","SWEPT_FACE",FACE,{"disambiguationData":[OSD([sQuery(id+"F7.wireOp",EDGE,"E32.bottom")])]});
            var sketch = newSketch(context, id + "F12", { "sketchPlane" : qUnion([Q0])});
            skLineSegment(sketch, "E57.bottom", {"start": v(-519.86, 699.7) * mm, "end": v(-495.5, 699.7) * mm});
            skLineSegment(sketch, "E57.top", {"start": v(-519.86, 675.52) * mm, "end": v(-495.5, 675.52) * mm});
            skLineSegment(sketch, "E57.left", {"start": v(-519.86, 699.7) * mm, "end": v(-519.86, 675.52) * mm});
            skLineSegment(sketch, "E57.right", {"start": v(-495.5, 699.7) * mm, "end": v(-495.5, 675.52) * mm});
            skLineSegment(sketch, "E58", {"start": v(0, 0) * mm, "end": v(0, 757.39) * mm, "construction": true});
            skLineSegment(sketch, "E59.MirrorCS", {"start": v(519.86, 699.7) * mm, "end": v(519.86, 675.52) * mm});
            skLineSegment(sketch, "E60.MirrorCS", {"start": v(495.5, 699.7) * mm, "end": v(495.5, 675.52) * mm});
            skLineSegment(sketch, "E61.MirrorCS", {"start": v(519.86, 699.7) * mm, "end": v(495.5, 699.7) * mm});
            skLineSegment(sketch, "E62.MirrorCS", {"start": v(519.86, 675.52) * mm, "end": v(495.5, 675.52) * mm});
            skSolve(sketch);
        }
        {
            var Q0;
            Q0 = qSketchRegion(id + "F12", true);
            extrude(context, id + "F13", {"entities" : qUnion([Q0]), "endBound" : BoundingType.UP_TO_NEXT, "depth" : 25.4 * mm});
        }
        {
            var Q0;
            Q0=qCreatedBy(makeId("Front.planeOp"),FACE);
            cPlane(context, id + "F14", {"entities" : qUnion([Q0]), "cplaneType" : CPlaneType.OFFSET, "offset" : 152.4 * mm, "oppositeDirection" : true, "width" : 152.4 * mm, "height" : 152.4 * mm});
        }
        {
            var Q0;
            Q0=qCreatedBy(id+"F14.planeOp",FACE);
            var sketch = newSketch(context, id + "F15", { "sketchPlane" : qUnion([Q0])});
            skCircle(sketch, "E63.cCircle", {"center": v(-0.97, 54.97) * mm, "radius": 25.4 * mm, "construction": true});
            skLineSegment(sketch, "E63.0", {"start": v(-2.04, 105.76) * mm, "end": v(43.54, 30.5) * mm});
            skLineSegment(sketch, "E63.1", {"start": v(43.54, 30.5) * mm, "end": v(-44.42, 28.65) * mm});
            skLineSegment(sketch, "E63.2", {"start": v(-44.42, 28.65) * mm, "end": v(-2.04, 105.76) * mm});
            skPoint(sketch, "E63.0.midPoint", {"position": v(20.75, 68.13) * mm});
            skCircle(sketch, "E64.cCircle", {"center": v(40.9, 132.9) * mm, "radius": 25.4 * mm, "construction": true});
            skLineSegment(sketch, "E64.0", {"start": v(39.89, 183.7) * mm, "end": v(85.4, 108.4) * mm});
            skLineSegment(sketch, "E64.1", {"start": v(85.4, 108.4) * mm, "end": v(-2.57, 106.63) * mm});
            skLineSegment(sketch, "E64.2", {"start": v(-2.57, 106.63) * mm, "end": v(39.89, 183.7) * mm});
            skPoint(sketch, "E64.0.midPoint", {"position": v(62.64, 146.05) * mm});
            skCircle(sketch, "E65.cCircle", {"center": v(-48.8, 132.34) * mm, "radius": 25.4 * mm, "construction": true});
            skLineSegment(sketch, "E65.0", {"start": v(-49.53, 183.14) * mm, "end": v(-4.46, 107.57) * mm});
            skLineSegment(sketch, "E65.1", {"start": v(-4.46, 107.57) * mm, "end": v(-92.44, 106.32) * mm});
            skLineSegment(sketch, "E65.2", {"start": v(-92.44, 106.32) * mm, "end": v(-49.53, 183.14) * mm});
            skPoint(sketch, "E65.0.midPoint", {"position": v(-27, 145.35) * mm});
            skCircle(sketch, "E66.cCircle", {"center": v(85.2, 211.26) * mm, "radius": 25.4 * mm, "construction": true});
            skLineSegment(sketch, "E66.0", {"start": v(84.1, 262.05) * mm, "end": v(129.72, 186.81) * mm});
            skLineSegment(sketch, "E66.1", {"start": v(129.72, 186.81) * mm, "end": v(41.75, 184.93) * mm});
            skLineSegment(sketch, "E66.2", {"start": v(41.75, 184.93) * mm, "end": v(84.1, 262.05) * mm});
            skPoint(sketch, "E66.0.midPoint", {"position": v(106.9, 224.43) * mm});
            skCircle(sketch, "E67.cCircle", {"center": v(38.16, 285.71) * mm, "radius": 25.4 * mm, "construction": true});
            skLineSegment(sketch, "E67.0", {"start": v(37.12, 336.5) * mm, "end": v(82.66, 261.22) * mm});
            skLineSegment(sketch, "E67.1", {"start": v(82.66, 261.22) * mm, "end": v(-5.3, 259.42) * mm});
            skLineSegment(sketch, "E67.2", {"start": v(-5.3, 259.42) * mm, "end": v(37.12, 336.5) * mm});
            skPoint(sketch, "E67.0.midPoint", {"position": v(59.9, 298.86) * mm});
            skCircle(sketch, "E68.cCircle", {"center": v(-5.93, 209.08) * mm, "radius": 25.4 * mm, "construction": true});
            skLineSegment(sketch, "E68.0", {"start": v(-6.93, 259.87) * mm, "end": v(38.56, 184.55) * mm});
            skLineSegment(sketch, "E68.1", {"start": v(38.56, 184.55) * mm, "end": v(-49.41, 182.81) * mm});
            skLineSegment(sketch, "E68.2", {"start": v(-49.41, 182.81) * mm, "end": v(-6.93, 259.87) * mm});
            skPoint(sketch, "E68.0.midPoint", {"position": v(15.81, 222.2) * mm});
            skCircle(sketch, "E69.cCircle", {"center": v(-54.06, 284.77) * mm, "radius": 25.4 * mm, "construction": true});
            skLineSegment(sketch, "E69.0", {"start": v(-55.37, 335.56) * mm, "end": v(-9.43, 260.51) * mm});
            skLineSegment(sketch, "E69.1", {"start": v(-9.43, 260.51) * mm, "end": v(-97.39, 258.25) * mm});
            skLineSegment(sketch, "E69.2", {"start": v(-97.39, 258.25) * mm, "end": v(-55.37, 335.56) * mm});
            skPoint(sketch, "E69.0.midPoint", {"position": v(-32.4, 298.04) * mm});
            skCircle(sketch, "E70.cCircle", {"center": v(-9.13, 365.51) * mm, "radius": 25.4 * mm, "construction": true});
            skLineSegment(sketch, "E70.0", {"start": v(-10.2, 416.3) * mm, "end": v(35.4, 341.04) * mm});
            skLineSegment(sketch, "E70.1", {"start": v(35.4, 341.04) * mm, "end": v(-52.58, 339.2) * mm});
            skLineSegment(sketch, "E70.2", {"start": v(-52.58, 339.2) * mm, "end": v(-10.2, 416.3) * mm});
            skPoint(sketch, "E70.0.midPoint", {"position": v(12.6, 378.67) * mm});
            skCircle(sketch, "E71.cCircle", {"center": v(-90.1, 51.72) * mm, "radius": 25.4 * mm, "construction": true});
            skLineSegment(sketch, "E71.0", {"start": v(-91.13, 102.5) * mm, "end": v(-45.6, 27.21) * mm});
            skLineSegment(sketch, "E71.1", {"start": v(-45.6, 27.21) * mm, "end": v(-133.57, 25.43) * mm});
            skLineSegment(sketch, "E71.2", {"start": v(-133.57, 25.43) * mm, "end": v(-91.13, 102.5) * mm});
            skPoint(sketch, "E71.0.midPoint", {"position": v(-68.36, 64.86) * mm});
            skCircle(sketch, "E72.cCircle", {"center": v(131.57, 133.7) * mm, "radius": 25.4 * mm, "construction": true});
            skLineSegment(sketch, "E72.0", {"start": v(130.4, 184.5) * mm, "end": v(176.14, 109.33) * mm});
            skLineSegment(sketch, "E72.1", {"start": v(176.14, 109.33) * mm, "end": v(88.18, 107.3) * mm});
            skLineSegment(sketch, "E72.2", {"start": v(88.18, 107.3) * mm, "end": v(130.4, 184.5) * mm});
            skPoint(sketch, "E72.0.midPoint", {"position": v(153.27, 146.91) * mm});
            skCircle(sketch, "E73.cCircle", {"center": v(-131.42, -25.45) * mm, "radius": 25.4 * mm, "construction": true});
            skLineSegment(sketch, "E73.0", {"start": v(-132.55, 25.33) * mm, "end": v(-86.87, -49.87) * mm});
            skLineSegment(sketch, "E73.1", {"start": v(-86.87, -49.87) * mm, "end": v(-174.84, -51.83) * mm});
            skLineSegment(sketch, "E73.2", {"start": v(-174.84, -51.83) * mm, "end": v(-132.55, 25.33) * mm});
            skPoint(sketch, "E73.0.midPoint", {"position": v(-109.71, -12.27) * mm});
            skCircle(sketch, "E74.cCircle", {"center": v(-220.34, -28.2) * mm, "radius": 25.4 * mm, "construction": true});
            skLineSegment(sketch, "E74.0", {"start": v(-221.5, 22.58) * mm, "end": v(-175.78, -52.6) * mm});
            skLineSegment(sketch, "E74.1", {"start": v(-175.78, -52.6) * mm, "end": v(-263.75, -54.6) * mm});
            skLineSegment(sketch, "E74.2", {"start": v(-263.75, -54.6) * mm, "end": v(-221.5, 22.58) * mm});
            skPoint(sketch, "E74.0.midPoint", {"position": v(-198.64, -15) * mm});
            skCircle(sketch, "E75.cCircle", {"center": v(-264.09, -106.41) * mm, "radius": 25.4 * mm, "construction": true});
            skLineSegment(sketch, "E75.0", {"start": v(-265.69, -55.64) * mm, "end": v(-219.31, -130.41) * mm});
            skLineSegment(sketch, "E75.1", {"start": v(-219.31, -130.41) * mm, "end": v(-307.26, -133.2) * mm});
            skLineSegment(sketch, "E75.2", {"start": v(-307.26, -133.2) * mm, "end": v(-265.69, -55.64) * mm});
            skPoint(sketch, "E75.0.midPoint", {"position": v(-242.5, -93.03) * mm});
            skCircle(sketch, "E76.cCircle", {"center": v(-400.25, -31.62) * mm, "radius": 25.4 * mm, "construction": true});
            skLineSegment(sketch, "E76.0", {"start": v(-401.3, 19.17) * mm, "end": v(-355.75, -56.11) * mm});
            skLineSegment(sketch, "E76.1", {"start": v(-355.75, -56.11) * mm, "end": v(-443.72, -57.92) * mm});
            skLineSegment(sketch, "E76.2", {"start": v(-443.72, -57.92) * mm, "end": v(-401.3, 19.17) * mm});
            skPoint(sketch, "E76.0.midPoint", {"position": v(-378.52, -18.47) * mm});
            skCircle(sketch, "E77.cCircle", {"center": v(-312.23, -29.6) * mm, "radius": 25.4 * mm, "construction": true});
            skLineSegment(sketch, "E77.0", {"start": v(-313.28, 21.2) * mm, "end": v(-267.73, -54.09) * mm});
            skLineSegment(sketch, "E77.1", {"start": v(-267.73, -54.09) * mm, "end": v(-355.7, -55.9) * mm});
            skLineSegment(sketch, "E77.2", {"start": v(-355.7, -55.9) * mm, "end": v(-313.28, 21.2) * mm});
            skPoint(sketch, "E77.0.midPoint", {"position": v(-290.5, -16.45) * mm});
            skCircle(sketch, "E78.cCircle", {"center": v(-354.93, -106.69) * mm, "radius": 25.4 * mm, "construction": true});
            skLineSegment(sketch, "E78.0", {"start": v(-355.7, -55.9) * mm, "end": v(-310.55, -131.42) * mm});
            skLineSegment(sketch, "E78.1", {"start": v(-310.55, -131.42) * mm, "end": v(-398.53, -132.75) * mm});
            skLineSegment(sketch, "E78.2", {"start": v(-398.53, -132.75) * mm, "end": v(-355.7, -55.9) * mm});
            skPoint(sketch, "E78.0.midPoint", {"position": v(-333.12, -93.66) * mm});
            skCircle(sketch, "E79.cCircle", {"center": v(-446.61, 44.87) * mm, "radius": 25.4 * mm, "construction": true});
            skLineSegment(sketch, "E79.0", {"start": v(-447.39, 95.66) * mm, "end": v(-402.23, 20.14) * mm});
            skLineSegment(sketch, "E79.1", {"start": v(-402.23, 20.14) * mm, "end": v(-490.21, 18.8) * mm});
            skLineSegment(sketch, "E79.2", {"start": v(-490.21, 18.8) * mm, "end": v(-447.39, 95.66) * mm});
            skPoint(sketch, "E79.0.midPoint", {"position": v(-424.81, 57.9) * mm});
            skCircle(sketch, "E80.cCircle", {"center": v(449.57, 67.08) * mm, "radius": 25.4 * mm, "construction": true});
            skLineSegment(sketch, "E80.0", {"start": v(448.77, 117.87) * mm, "end": v(493.96, 42.38) * mm});
            skLineSegment(sketch, "E80.1", {"start": v(493.96, 42.38) * mm, "end": v(405.99, 40.98) * mm});
            skLineSegment(sketch, "E80.2", {"start": v(405.99, 40.98) * mm, "end": v(448.77, 117.87) * mm});
            skPoint(sketch, "E80.0.midPoint", {"position": v(471.37, 80.13) * mm});
            skCircle(sketch, "E81.cCircle", {"center": v(403.66, 143.38) * mm, "radius": 25.4 * mm, "construction": true});
            skLineSegment(sketch, "E81.0", {"start": v(403.29, 194.18) * mm, "end": v(447.84, 118.3) * mm});
            skLineSegment(sketch, "E81.1", {"start": v(447.84, 118.3) * mm, "end": v(359.85, 117.66) * mm});
            skLineSegment(sketch, "E81.2", {"start": v(359.85, 117.66) * mm, "end": v(403.29, 194.18) * mm});
            skPoint(sketch, "E81.0.midPoint", {"position": v(425.56, 156.24) * mm});
            skCircle(sketch, "E82.cCircle", {"center": v(362.47, 66.4) * mm, "radius": 25.4 * mm, "construction": true});
            skLineSegment(sketch, "E82.0", {"start": v(361.52, 117.2) * mm, "end": v(406.93, 41.83) * mm});
            skLineSegment(sketch, "E82.1", {"start": v(406.93, 41.83) * mm, "end": v(318.96, 40.18) * mm});
            skLineSegment(sketch, "E82.2", {"start": v(318.96, 40.18) * mm, "end": v(361.52, 117.2) * mm});
            skPoint(sketch, "E82.0.midPoint", {"position": v(384.22, 79.51) * mm});
            skCircle(sketch, "E83.cCircle", {"center": v(274.02, 63.7) * mm, "radius": 25.4 * mm, "construction": true});
            skLineSegment(sketch, "E83.0", {"start": v(272.8, 114.49) * mm, "end": v(318.6, 39.37) * mm});
            skLineSegment(sketch, "E83.1", {"start": v(318.6, 39.37) * mm, "end": v(230.64, 37.25) * mm});
            skLineSegment(sketch, "E83.2", {"start": v(230.64, 37.25) * mm, "end": v(272.8, 114.49) * mm});
            skPoint(sketch, "E83.0.midPoint", {"position": v(295.7, 76.93) * mm});
            skCircle(sketch, "E84.cCircle", {"center": v(404.59, -11.24) * mm, "radius": 25.4 * mm, "construction": true});
            skLineSegment(sketch, "E84.0", {"start": v(405.96, 39.55) * mm, "end": v(447.88, -37.81) * mm});
            skLineSegment(sketch, "E84.1", {"start": v(447.88, -37.81) * mm, "end": v(359.92, -35.44) * mm});
            skLineSegment(sketch, "E84.2", {"start": v(359.92, -35.44) * mm, "end": v(405.96, 39.55) * mm});
            skPoint(sketch, "E84.0.midPoint", {"position": v(426.92, 0.87) * mm});
            skCircle(sketch, "E85.cCircle", {"center": v(444.55, -90.84) * mm, "radius": 25.4 * mm, "construction": true});
            skLineSegment(sketch, "E85.0", {"start": v(443.86, -40.04) * mm, "end": v(488.88, -115.64) * mm});
            skLineSegment(sketch, "E85.1", {"start": v(488.88, -115.64) * mm, "end": v(400.9, -116.83) * mm});
            skLineSegment(sketch, "E85.2", {"start": v(400.9, -116.83) * mm, "end": v(443.86, -40.04) * mm});
            skPoint(sketch, "E85.0.midPoint", {"position": v(466.37, -77.84) * mm});
            skSolve(sketch);
        }
        {
            var Q0;
            Q0=makeQuery(id+"F15.imprint","IMPRINT",FACE,{"disambiguationData":[TD([[makeQuery(id+"F15.imprint","IMPRINT",EDGE,{"derivedFrom":sQuery(id+"F15.wireOp",EDGE,"E79.0")}),-1.0]])]});
            var Q1;
            {var subQ0=sQuery(id+"F15.wireOp",EDGE,"E76.2");Q1=makeQuery(id+"F15.imprint","IMPRINT",FACE,{"disambiguationData":[TD([[makeQuery(id+"F15.imprint","IMPRINT",EDGE,{"derivedFrom":subQ0}),-1.0]])]});}
            var Q2;
            Q2=makeQuery(id+"F15.imprint","IMPRINT",FACE,{"disambiguationData":[TD([[makeQuery(id+"F15.imprint","IMPRINT",EDGE,{"derivedFrom":sQuery(id+"F15.wireOp",EDGE,"E77.0")}),-1.0]])]});
            var Q3;
            Q3=makeQuery(id+"F15.imprint","IMPRINT",FACE,{"disambiguationData":[TD([[makeQuery(id+"F15.imprint","IMPRINT",EDGE,{"derivedFrom":sQuery(id+"F15.wireOp",EDGE,"E74.0")}),-1.0]])]});
            var Q4;
            Q4=makeQuery(id+"F15.imprint","IMPRINT",FACE,{"disambiguationData":[TD([[makeQuery(id+"F15.imprint","IMPRINT",EDGE,{"derivedFrom":sQuery(id+"F15.wireOp",EDGE,"E73.0")}),-1.0]])]});
            var Q5;
            Q5=makeQuery(id+"F15.imprint","IMPRINT",FACE,{"disambiguationData":[TD([[makeQuery(id+"F15.imprint","IMPRINT",EDGE,{"derivedFrom":sQuery(id+"F15.wireOp",EDGE,"E75.0")}),-1.0]])]});
            var Q6;
            {var subQ0=sQuery(id+"F15.wireOp",EDGE,"E78.0");Q6=makeQuery(id+"F15.imprint","IMPRINT",FACE,{"disambiguationData":[TD([[makeQuery(id+"F15.imprint","IMPRINT",EDGE,{"derivedFrom":subQ0}),-1.0]])]});}
            var Q7;
            Q7=makeQuery(id+"F15.imprint","IMPRINT",FACE,{"disambiguationData":[TD([[makeQuery(id+"F15.imprint","IMPRINT",EDGE,{"derivedFrom":sQuery(id+"F15.wireOp",EDGE,"E71.0")}),-1.0]])]});
            var Q8;
            Q8=makeQuery(id+"F15.imprint","IMPRINT",FACE,{"disambiguationData":[TD([[makeQuery(id+"F15.imprint","IMPRINT",EDGE,{"derivedFrom":sQuery(id+"F15.wireOp",EDGE,"E63.0")}),-1.0]])]});
            var Q9;
            {var subQ1=sQuery(id+"F15.wireOp",EDGE,"E65.1");Q9=makeQuery(id+"F15.imprint","IMPRINT",FACE,{"disambiguationData":[TD([[makeQuery(id+"F15.imprint","IMPRINT",EDGE,{"derivedFrom":subQ1}),-1.0]])]});}
            var Q10;
            Q10=makeQuery(id+"F15.imprint","IMPRINT",FACE,{"disambiguationData":[TD([[makeQuery(id+"F15.imprint","IMPRINT",EDGE,{"derivedFrom":sQuery(id+"F15.wireOp",EDGE,"E64.0")}),-1.0]])]});
            var Q11;
            Q11=makeQuery(id+"F15.imprint","IMPRINT",FACE,{"disambiguationData":[TD([[makeQuery(id+"F15.imprint","IMPRINT",EDGE,{"derivedFrom":sQuery(id+"F15.wireOp",EDGE,"E72.0")}),-1.0]])]});
            var Q12;
            Q12=makeQuery(id+"F15.imprint","IMPRINT",FACE,{"disambiguationData":[TD([[makeQuery(id+"F15.imprint","IMPRINT",EDGE,{"derivedFrom":sQuery(id+"F15.wireOp",EDGE,"E66.0")}),-1.0]])]});
            var Q13;
            {var subQ5=sQuery(id+"F15.wireOp",EDGE,"E68.0");Q13=makeQuery(id+"F15.imprint","IMPRINT",FACE,{"disambiguationData":[TD([[makeQuery(id+"F15.imprint","IMPRINT",EDGE,{"derivedFrom":subQ5}),-1.0]])]});}
            var Q14;
            Q14=makeQuery(id+"F15.imprint","IMPRINT",FACE,{"disambiguationData":[TD([[makeQuery(id+"F15.imprint","IMPRINT",EDGE,{"derivedFrom":sQuery(id+"F15.wireOp",EDGE,"E67.0")}),-1.0]])]});
            var Q15;
            Q15=makeQuery(id+"F15.imprint","IMPRINT",FACE,{"disambiguationData":[TD([[makeQuery(id+"F15.imprint","IMPRINT",EDGE,{"derivedFrom":sQuery(id+"F15.wireOp",EDGE,"E69.0")}),-1.0]])]});
            var Q16;
            Q16=makeQuery(id+"F15.imprint","IMPRINT",FACE,{"disambiguationData":[TD([[makeQuery(id+"F15.imprint","IMPRINT",EDGE,{"derivedFrom":sQuery(id+"F15.wireOp",EDGE,"E70.0")}),-1.0]])]});
            var Q17;
            Q17=makeQuery(id+"F15.imprint","IMPRINT",FACE,{"disambiguationData":[TD([[makeQuery(id+"F15.imprint","IMPRINT",EDGE,{"derivedFrom":sQuery(id+"F15.wireOp",EDGE,"E83.0")}),-1.0]])]});
            var Q18;
            Q18=makeQuery(id+"F15.imprint","IMPRINT",FACE,{"disambiguationData":[TD([[makeQuery(id+"F15.imprint","IMPRINT",EDGE,{"derivedFrom":sQuery(id+"F15.wireOp",EDGE,"E81.0")}),-1.0]])]});
            var Q19;
            {var subQ1=sQuery(id+"F15.wireOp",EDGE,"E80.0");Q19=makeQuery(id+"F15.imprint","IMPRINT",FACE,{"disambiguationData":[TD([[makeQuery(id+"F15.imprint","IMPRINT",EDGE,{"derivedFrom":subQ1}),-1.0]])]});}
            var Q20;
            {var subQ5=sQuery(id+"F15.wireOp",EDGE,"E82.2");Q20=makeQuery(id+"F15.imprint","IMPRINT",FACE,{"disambiguationData":[TD([[makeQuery(id+"F15.imprint","IMPRINT",EDGE,{"derivedFrom":subQ5}),-1.0]])]});}
            var Q21;
            Q21=makeQuery(id+"F15.imprint","IMPRINT",FACE,{"disambiguationData":[TD([[makeQuery(id+"F15.imprint","IMPRINT",EDGE,{"derivedFrom":sQuery(id+"F15.wireOp",EDGE,"E84.0")}),-1.0]])]});
            var Q22;
            Q22=makeQuery(id+"F15.imprint","IMPRINT",FACE,{"disambiguationData":[TD([[makeQuery(id+"F15.imprint","IMPRINT",EDGE,{"derivedFrom":sQuery(id+"F15.wireOp",EDGE,"E85.0")}),-1.0]])]});
            extrude(context, id + "F16", {"entities" : qUnion([Q0, Q1, Q2, Q3, Q4, Q5, Q6, Q7, Q8, Q9, Q10, Q11, Q12, Q13, Q14, Q15, Q16, Q17, Q18, Q19, Q20, Q21, Q22]), "depth" : 3 * mm});
        }
        {
            var Q0;
            Q0=makeQuery(id+"F4.opExtrude","SWEPT_FACE",FACE,{"disambiguationData":[OSD([sQuery(id+"F3.wireOp",EDGE,"E22.MirrorCS")])]});
            var sketch = newSketch(context, id + "F17", { "sketchPlane" : qUnion([Q0])});
            skLineSegment(sketch, "E86.bottom", {"start": v(495, 488.12) * mm, "end": v(-494.97, 488.12) * mm});
            skLineSegment(sketch, "E86.top", {"start": v(495, 485.12) * mm, "end": v(-494.97, 485.12) * mm});
            skLineSegment(sketch, "E86.left", {"start": v(495, 488.12) * mm, "end": v(495, 485.12) * mm});
            skLineSegment(sketch, "E86.right", {"start": v(-494.97, 488.12) * mm, "end": v(-494.97, 485.12) * mm});
            skSolve(sketch);
        }
        {
            var Q0;
            Q0 = qSketchRegion(id + "F17", true);
            extrude(context, id + "F18", {"entities" : qUnion([Q0]), "operationType" : NewBodyOperationType.ADD, "oppositeDirection" : true, "depth" : 3 * mm});
        }
        {
            var Q0;
            Q0=makeQuery(id+"F8.opExtrude","SWEPT_FACE",FACE,{"disambiguationData":[OSD([sQuery(id+"F7.wireOp",EDGE,"E35.MirrorCS")])]});
            var sketch = newSketch(context, id + "F19", { "sketchPlane" : qUnion([Q0])});
            skLineSegment(sketch, "E87.0.0", {"start": v(-495, 488.12) * mm, "end": v(-495, 485.12) * mm});
            skLineSegment(sketch, "E87.0.1", {"start": v(-495, 485.12) * mm, "end": v(494.97, 485.12) * mm});
            skLineSegment(sketch, "E87.0.2", {"start": v(494.97, 485.12) * mm, "end": v(494.97, 488.12) * mm});
            skLineSegment(sketch, "E87.0.3", {"start": v(494.97, 488.12) * mm, "end": v(-495, 488.12) * mm});
            skSolve(sketch);
        }
        {
            var Q0;
            Q0=makeQuery(id+"F19.imprint","IMPRINT",FACE,{"disambiguationData":[TD([[makeQuery(id+"F19.imprint","IMPRINT",EDGE,{"derivedFrom":sQuery(id+"F19.wireOp",EDGE,"E87.0.0")}),1.0]])]});
            extrude(context, id + "F20", {"entities" : qUnion([Q0]), "oppositeDirection" : true, "depth" : 3 * mm});
        }
        {
            var Q0;
            Q0=makeQuery(id+"F8.opExtrude","SWEPT_FACE",FACE,{"disambiguationData":[OSD([sQuery(id+"F7.wireOp",EDGE,"E37.MirrorCS")])]});
            var sketch = newSketch(context, id + "F21", { "sketchPlane" : qUnion([Q0])});
            skLineSegment(sketch, "E88.bottom", {"start": v(9.33, -36.13) * mm, "end": v(308.03, -36.13) * mm});
            skLineSegment(sketch, "E88.top", {"start": v(9.33, -39.13) * mm, "end": v(308.03, -39.13) * mm});
            skLineSegment(sketch, "E88.left", {"start": v(9.33, -36.13) * mm, "end": v(9.33, -39.13) * mm});
            skLineSegment(sketch, "E88.right", {"start": v(308.03, -36.13) * mm, "end": v(308.03, -39.13) * mm});
            skSolve(sketch);
        }
        {
            var Q0;
            Q0 = qSketchRegion(id + "F21", true);
            extrude(context, id + "F22", {"entities" : qUnion([Q0]), "operationType" : NewBodyOperationType.ADD, "oppositeDirection" : true, "depth" : 3 * mm});
        }
        {
            var Q0;
            Q0=makeQuery(id+"F4.opExtrude","SWEPT_FACE",FACE,{"disambiguationData":[OSD([sQuery(id+"F3.wireOp",EDGE,"E20.left")])]});
            var sketch = newSketch(context, id + "F23", { "sketchPlane" : qUnion([Q0])});
            skLineSegment(sketch, "E89.0.0", {"start": v(-9.33, -36.13) * mm, "end": v(-308.03, -36.13) * mm});
            skLineSegment(sketch, "E89.0.1", {"start": v(-308.03, -36.13) * mm, "end": v(-308.03, -39.13) * mm});
            skLineSegment(sketch, "E89.0.2", {"start": v(-308.03, -39.13) * mm, "end": v(-9.33, -39.13) * mm});
            skLineSegment(sketch, "E89.0.3", {"start": v(-9.33, -39.13) * mm, "end": v(-9.33, -36.13) * mm});
            skSolve(sketch);
        }
        {
            var Q0;
            Q0=makeQuery(id+"F23.imprint","IMPRINT",FACE,{"disambiguationData":[TD([[makeQuery(id+"F23.imprint","IMPRINT",EDGE,{"derivedFrom":sQuery(id+"F23.wireOp",EDGE,"E89.0.0")}),1.0]])]});
            extrude(context, id + "F24", {"entities" : qUnion([Q0]), "operationType" : NewBodyOperationType.ADD, "oppositeDirection" : true, "depth" : 3 * mm});
        }
        {
            var Q0;
            Q0=qCreatedBy(makeId("Front.planeOp"),FACE);
            var sketch = newSketch(context, id + "F25", { "sketchPlane" : qUnion([Q0])});
            skLineSegment(sketch, "E90", {"start": v(-493.84, -84.8) * mm, "end": v(-320.86, -84.8) * mm});
            skLineSegment(sketch, "E91", {"start": v(-320.86, -84.8) * mm, "end": v(-243.8, 47.4) * mm});
            skLineSegment(sketch, "E92", {"start": v(-243.8, 47.4) * mm, "end": v(-140.05, 47.4) * mm});
            skLineSegment(sketch, "E93", {"start": v(-140.05, 47.4) * mm, "end": v(-186.82, -45.22) * mm});
            skLineSegment(sketch, "E94", {"start": v(-186.82, -45.22) * mm, "end": v(-294.32, -45.22) * mm});
            skLineSegment(sketch, "E95.0", {"start": v(-188.66, -42.22) * mm, "end": v(-292.57, -42.22) * mm});
            skLineSegment(sketch, "E95.1", {"start": v(-144.93, 44.4) * mm, "end": v(-188.66, -42.22) * mm});
            skLineSegment(sketch, "E95.2", {"start": v(-242.22, 44.4) * mm, "end": v(-144.93, 44.4) * mm});
            skLineSegment(sketch, "E96.0", {"start": v(-319.14, -87.8) * mm, "end": v(-294.32, -45.22) * mm});
            skLineSegment(sketch, "E96.1", {"start": v(-493.8, -87.8) * mm, "end": v(-319.14, -87.8) * mm});
            skLineSegment(sketch, "E97", {"start": v(-493.84, -84.8) * mm, "end": v(-493.8, -87.8) * mm});
            skLineSegment(sketch, "E98.trimOffspring", {"start": v(-292.57, -42.22) * mm, "end": v(-242.08, 44.4) * mm});
            skLineSegment(sketch, "E99", {"start": v(-140.05, 47.4) * mm, "end": v(-211.53, 194.59) * mm});
            skLineSegment(sketch, "E100", {"start": v(-211.53, 194.59) * mm, "end": v(-67.87, 194.59) * mm});
            skLineSegment(sketch, "E101", {"start": v(-67.87, 194.59) * mm, "end": v(-140.05, 47.4) * mm});
            skLineSegment(sketch, "E102.0", {"start": v(-206.74, 191.59) * mm, "end": v(-72.69, 191.59) * mm});
            skLineSegment(sketch, "E102.1", {"start": v(-140.04, 54.25) * mm, "end": v(-206.74, 191.59) * mm});
            skLineSegment(sketch, "E102.2", {"start": v(-72.69, 191.59) * mm, "end": v(-140.04, 54.25) * mm});
            skLineSegment(sketch, "E103", {"start": v(318.9, 289.96) * mm, "end": v(304.15, 133.6) * mm});
            skLineSegment(sketch, "E104", {"start": v(304.15, 133.6) * mm, "end": v(410.04, 133.6) * mm});
            skLineSegment(sketch, "E105.0", {"start": v(300.86, 130.6) * mm, "end": v(415.26, 130.6) * mm});
            skLineSegment(sketch, "E105.1", {"start": v(316.8, 299.54) * mm, "end": v(300.86, 130.6) * mm});
            skLineSegment(sketch, "E105.2", {"start": v(415.26, 130.6) * mm, "end": v(316.8, 299.54) * mm});
            skLineSegment(sketch, "E106", {"start": v(316.8, 299.54) * mm, "end": v(0, 299.54) * mm});
            skLineSegment(sketch, "E107.0", {"start": v(316.54, 296.54) * mm, "end": v(0, 296.54) * mm});
            skLineSegment(sketch, "E108", {"start": v(0, 299.54) * mm, "end": v(0, 296.54) * mm});
            skLineSegment(sketch, "E109", {"start": v(0, 296.54) * mm, "end": v(98.72, 120.53) * mm});
            skLineSegment(sketch, "E110", {"start": v(98.72, 120.53) * mm, "end": v(-80.48, 120.53) * mm});
            skLineSegment(sketch, "E111", {"start": v(-80.48, 120.53) * mm, "end": v(0, 299.54) * mm});
            skLineSegment(sketch, "E112.0", {"start": v(-75.85, 123.53) * mm, "end": v(-0.45, 291.22) * mm});
            skLineSegment(sketch, "E112.1", {"start": v(93.6, 123.53) * mm, "end": v(-75.85, 123.53) * mm});
            skLineSegment(sketch, "E112.2", {"start": v(-0.45, 291.22) * mm, "end": v(93.6, 123.53) * mm});
            skLineSegment(sketch, "E113.trimOffspring", {"start": v(410.04, 133.6) * mm, "end": v(318.9, 289.96) * mm});
            skSolve(sketch);
        }
        {
            var Q0;
            {var subQ6=sQuery(id+"F25.wireOp",EDGE,"E90");Q0=makeQuery(id+"F25.imprint","IMPRINT",FACE,{"disambiguationData":[TD([[makeQuery(id+"F25.imprint","IMPRINT",EDGE,{"derivedFrom":subQ6}),-1.0]])]});}
            var Q1;
            {var subQ10=sQuery(id+"F25.wireOp",EDGE,"E92");Q1=makeQuery(id+"F25.imprint","IMPRINT",FACE,{"disambiguationData":[TD([[makeQuery(id+"F25.imprint","IMPRINT",EDGE,{"derivedFrom":subQ10}),-1.0]])]});}
            extrude(context, id + "F26", {"entities" : qUnion([Q0, Q1]), "operationType" : NewBodyOperationType.ADD, "depth" : 3 * mm});
        }
        {
            var Q0;
            Q0 = qSketchRegion(id + "F25", true);
            extrude(context, id + "F27", {"entities" : qUnion([Q0]), "depth" : 3 * mm});
        }
        {
            var Q0;
            Q0=makeQuery(id+"F8.opExtrude","SWEPT_FACE",FACE,{"disambiguationData":[OSD([sQuery(id+"F5.wireOp",EDGE,"E26.bottom")])]});
            var sketch = newSketch(context, id + "F28", { "sketchPlane" : qUnion([Q0])});
            skCircle(sketch, "E114.cCircle", {"center": v(249.7, 21.63) * mm, "radius": 45.16 * mm, "construction": true});
            skLineSegment(sketch, "E114.0", {"start": v(171.48, -23.53) * mm, "end": v(249.7, 111.94) * mm});
            skLineSegment(sketch, "E114.1", {"start": v(249.7, 111.94) * mm, "end": v(327.92, -23.53) * mm});
            skLineSegment(sketch, "E114.2", {"start": v(327.92, -23.53) * mm, "end": v(171.48, -23.53) * mm});
            skPoint(sketch, "E114.0.midPoint", {"position": v(210.6, 44.2) * mm});
            skLineSegment(sketch, "E115.0", {"start": v(249.7, 117.94) * mm, "end": v(333.11, -26.53) * mm});
            skLineSegment(sketch, "E115.1", {"start": v(166.29, -26.53) * mm, "end": v(249.7, 117.94) * mm});
            skLineSegment(sketch, "E115.2", {"start": v(333.11, -26.53) * mm, "end": v(166.29, -26.53) * mm});
            skLineSegment(sketch, "E116.bottom", {"start": v(333.11, -26.53) * mm, "end": v(495.5, -26.53) * mm});
            skLineSegment(sketch, "E116.top", {"start": v(333.11, -23.53) * mm, "end": v(495.5, -23.53) * mm});
            skLineSegment(sketch, "E116.left", {"start": v(333.11, -26.53) * mm, "end": v(333.11, -23.53) * mm});
            skLineSegment(sketch, "E116.right", {"start": v(495.5, -26.53) * mm, "end": v(495.5, -23.53) * mm});
            skCircle(sketch, "E117.cCircle", {"center": v(-341.78, 288.02) * mm, "radius": 52.81 * mm, "construction": true});
            skLineSegment(sketch, "E117.0", {"start": v(-250.3, 340.83) * mm, "end": v(-341.78, 182.39) * mm});
            skLineSegment(sketch, "E117.1", {"start": v(-341.78, 182.39) * mm, "end": v(-433.26, 340.83) * mm});
            skLineSegment(sketch, "E117.2", {"start": v(-433.26, 340.83) * mm, "end": v(-250.3, 340.83) * mm});
            skPoint(sketch, "E117.0.midPoint", {"position": v(-296.04, 261.61) * mm});
            skLineSegment(sketch, "E118.0", {"start": v(-248.1, 338.64) * mm, "end": v(-340.28, 178.99) * mm});
            skLineSegment(sketch, "E118.1", {"start": v(-438.45, 343.83) * mm, "end": v(-245.1, 343.83) * mm});
            skLineSegment(sketch, "E118.2", {"start": v(-341.78, 176.39) * mm, "end": v(-436.72, 340.83) * mm});
            skLineSegment(sketch, "E119.bottom", {"start": v(-245.1, 343.83) * mm, "end": v(-492.69, 343.83) * mm});
            skLineSegment(sketch, "E119.left", {"start": v(-245.1, 343.83) * mm, "end": v(-245.1, 340.83) * mm});
            skLineSegment(sketch, "E119.right", {"start": v(-492.69, 343.83) * mm, "end": v(-492.69, 340.83) * mm});
            skLineSegment(sketch, "E120.top", {"start": v(-245.1, 126.58) * mm, "end": v(-248.1, 126.58) * mm});
            skLineSegment(sketch, "E120.left", {"start": v(-245.1, 340.83) * mm, "end": v(-245.1, 126.58) * mm});
            skLineSegment(sketch, "E120.right", {"start": v(-248.1, 338.64) * mm, "end": v(-248.1, 129.98) * mm});
            skLineSegment(sketch, "E121", {"start": v(-341.78, 176.39) * mm, "end": v(-248.1, 126.58) * mm});
            skLineSegment(sketch, "E122.0", {"start": v(-340.37, 179.04) * mm, "end": v(-248.1, 129.98) * mm});
            skLineSegment(sketch, "E123.trimOffspring", {"start": v(-436.72, 340.83) * mm, "end": v(-492.69, 340.83) * mm});
            skLineSegment(sketch, "E124.trimOffspring", {"start": v(-250.3, 340.83) * mm, "end": v(-433.26, 340.83) * mm});
            skSolve(sketch);
        }
        {
            var Q0;
            Q0 = qSketchRegion(id + "F28", true);
            extrude(context, id + "F29", {"entities" : qUnion([Q0]), "oppositeDirection" : true, "depth" : 3 * mm});
        }
    });
